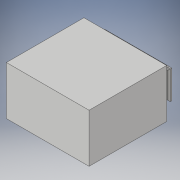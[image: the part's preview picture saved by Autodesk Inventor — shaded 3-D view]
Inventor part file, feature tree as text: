
AUTODESK INVENTOR PART (.ipt)
format: ipt  version: 2019 (Build 230136000, 136)  size: 116,736 bytes
history: native  units: mm
features: extrude x3, sketch x3, chamfer x1
ambient origin geometry x8: Origin, YZ Plane, XZ Plane, XY Plane, X Axis, Y Axis, Z Axis, Center Point
bodies: Solid1 (feature_tree)
feature tree (7):
  extrude  "Extrusion1"  Depth=18.3mm
  extrude  "Extrusion2"  Depth=38.3mm
  chamfer  "Chamfer1"  Distance=2.5mm
  extrude  "Extrusion3"  Depth=2.0mm TaperAngle=45.0deg
  sketch  "Sketch1"  dims[d0=43.3mm d1=18.3mm]
  sketch  "Sketch2"  dims[d2=2.0mm d3=0.0mm d4=38.3mm]
  sketch  "Sketch3"  dims[d5=11.8mm d6=2.5mm d7=0.0mm d8=1.0mm d9=2.0mm d10=45.0deg d11=53.3mm d12=7.5mm d13=12.0mm d14=50.0mm d15=0.0mm]
